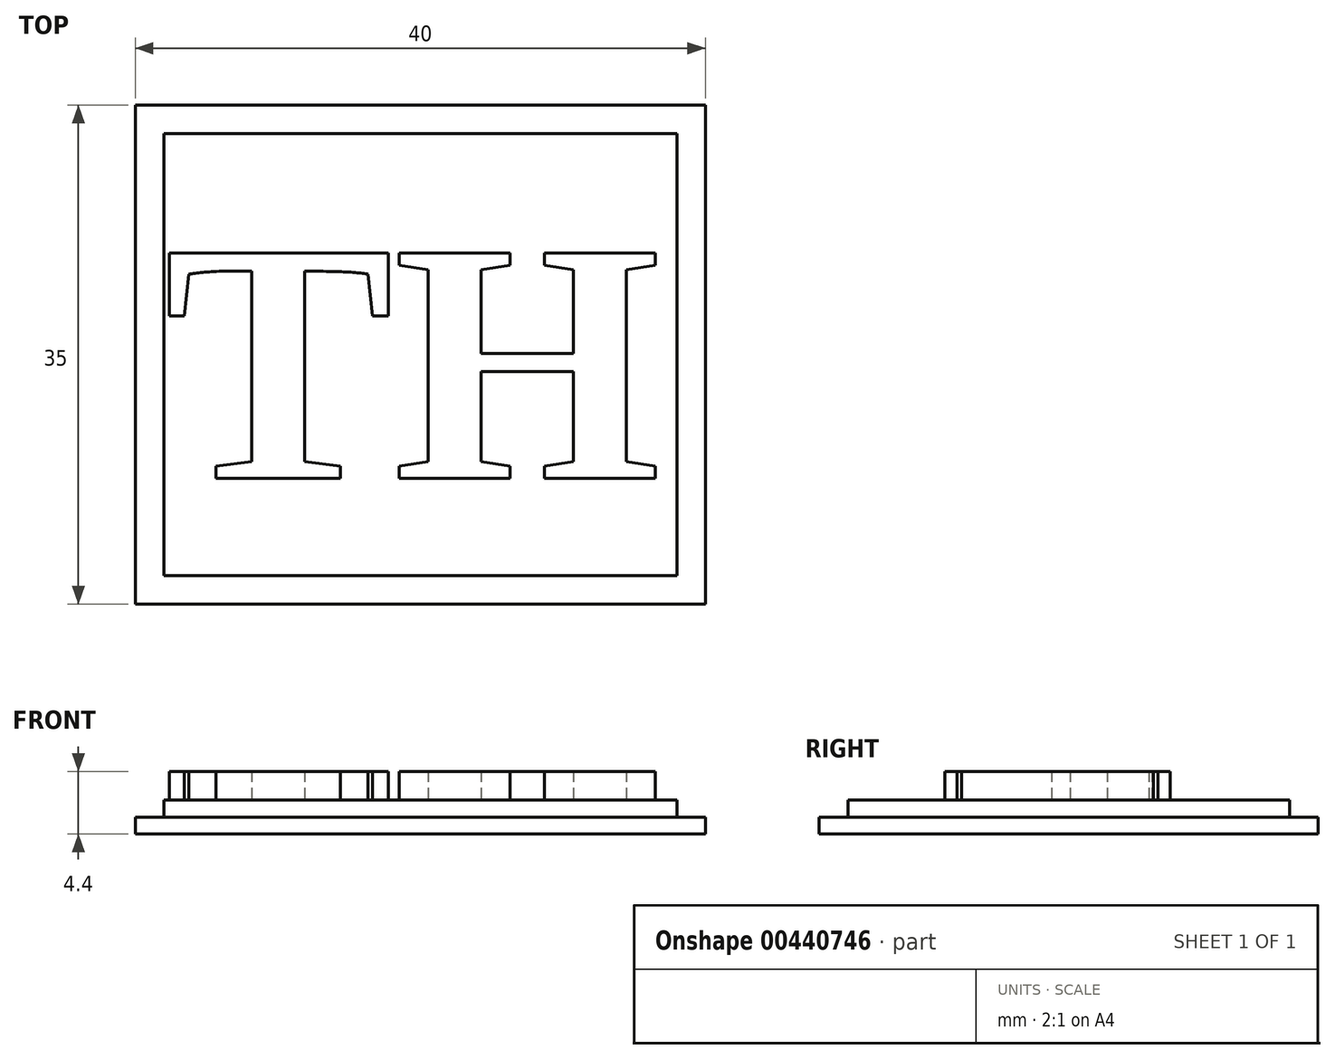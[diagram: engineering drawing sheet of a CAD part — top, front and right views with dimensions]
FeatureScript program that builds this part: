
annotation { "Feature Type Name" : "Feature", "Feature Type Description" : "" }
export const myFeature = defineFeature(function(context is Context, id is Id, definition is map)
    precondition{}
    {
        {
            var Q0;
            Q0=qCreatedBy(makeId("Top.planeOp"),FACE);
            var sketch = newSketch(context, id + "F0", { "sketchPlane" : qUnion([Q0])});
            skLineSegment(sketch, "E0.bottom", {"start": v(0, 0) * mm, "end": v(40, 0) * mm});
            skLineSegment(sketch, "E0.top", {"start": v(0, 35) * mm, "end": v(40, 35) * mm});
            skLineSegment(sketch, "E0.left", {"start": v(0, 0) * mm, "end": v(0, 35) * mm});
            skLineSegment(sketch, "E0.right", {"start": v(40, 0) * mm, "end": v(40, 35) * mm});
            skSolve(sketch);
        }
        {
            var Q0;
            Q0=qSketchRegion(id+"F0",true);
            extrude(context, id + "F1", {"entities" : qUnion([Q0]), "depth" : 1.2 * mm});
        }
        {
            var Q0;
            Q0=makeQuery(id+"F1.opExtrude","CAP_FACE",FACE,{"disambiguationData":[OSD([sQuery(id+"F0.wireOp",EDGE,"E0.bottom"),sQuery(id+"F0.wireOp",EDGE,"E0.top"),sQuery(id+"F0.wireOp",EDGE,"E0.left"),sQuery(id+"F0.wireOp",EDGE,"E0.right")])],"isStart":false});
            var sketch = newSketch(context, id + "F2", { "sketchPlane" : qUnion([Q0])});
            skLineSegment(sketch, "E1.0", {"start": v(38, 33) * mm, "end": v(2, 33) * mm});
            skLineSegment(sketch, "E1.1", {"start": v(38, 2) * mm, "end": v(38, 33) * mm});
            skLineSegment(sketch, "E1.2", {"start": v(2, 2) * mm, "end": v(38, 2) * mm});
            skLineSegment(sketch, "E1.3", {"start": v(2, 33) * mm, "end": v(2, 2) * mm});
            skSolve(sketch);
        }
        {
            var Q0;
            Q0=makeQuery(id+"F2.imprint","IMPRINT",FACE,{"disambiguationData":[TD([[makeQuery(id+"F2.imprint","IMPRINT",EDGE,{"derivedFrom":sQuery(id+"F2.wireOp",EDGE,"E1.0")}),1.0]])]});
            extrude(context, id + "F3", {"entities" : qUnion([Q0]), "operationType" : NewBodyOperationType.ADD, "depth" : 1.2 * mm});
        }
        {
            var Q0;
            Q0=makeQuery(id+"F3.opExtrude","CAP_FACE",FACE,{"disambiguationData":[OSD([sQuery(id+"F2.wireOp",EDGE,"E1.0"),sQuery(id+"F2.wireOp",EDGE,"E1.1"),sQuery(id+"F2.wireOp",EDGE,"E1.2"),sQuery(id+"F2.wireOp",EDGE,"E1.3")])],"isStart":false});
            var sketch = newSketch(context, id + "F4", { "sketchPlane" : qUnion([Q0])});
            skText(sketch, "E2", { "text": "TH", "fontName": "Tinos-Bold.ttf"});
            const initialGuessF4  = {"E2": [0.002, 0.00881, 1, 0, 0.01739]};
            skSetInitialGuess(sketch, initialGuessF4);
            skSolve(sketch);
        }
        {
            var Q0;
            Q0 = qSketchRegion(id + "F4", true);
            extrude(context, id + "F5", {"entities" : qUnion([Q0]), "operationType" : NewBodyOperationType.ADD, "depth" : 2 * mm});
        }
    });
